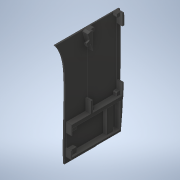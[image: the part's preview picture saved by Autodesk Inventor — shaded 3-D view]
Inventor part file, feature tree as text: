
AUTODESK INVENTOR PART (.ipt)
format: ipt  version: 2020.1 (Build 241239000, 239)  size: 1,676,800 bytes
history: native  units: mm
features: extrude x9, sketch x7, other x4, projected_geometry x3, split x1, chamfer x1, surface_op x1
ambient origin geometry x8: Origin, YZ Plane, XZ Plane, XY Plane, X Axis, Y Axis, Z Axis, Center Point
bodies: Solid1 (feature_tree)
feature tree (26):
  other  "Remote Bottom Shell.ipt"
  sketch  "Sketch1"  dims[d0=10.0mm d1=18.1mm]
  extrude  "Extrusion2"  Depth=10.0mm
  extrude  "Extrusion4"  Depth=29.5mm
  sketch  "Sketch3"  dims[d2=43.6mm d5=29.5mm]
  extrude  "Extrusion5"  Depth=2.0mm
  extrude  "Extrusion6"  Depth=1.2mm
  extrude  "Extrusion7"  Depth=1.2mm
  split  "Split1"
  extrude  "Extrusion8"  Depth=1.4mm
  extrude  "Extrusion9"  Depth=10.0mm
  extrude  "Extrusion10"  Depth=10.0mm TaperAngle=0.0deg
  chamfer  "Chamfer1"  Distance=3.5mm
  extrude  "Extrusion11"  Depth=10.0mm
  other  "Plate Solid::Remote Bottom Shell.ipt"
  other  "TaggingFeature1"
  projected_geometry  "Projected Loop1"
  sketch  "Sketch4"  dims[d6=15.35mm d7=2.0mm]
  sketch  "Sketch5"  dims[d8=0.2mm d9=0.0mm d17=1.2mm]
  projected_geometry  "Projected Loop2"
  projected_geometry  "Projected Loop3"
  sketch  "Sketch6"  dims[d18=1.2mm d21=30.0mm]
  sketch  "Sketch7"  dims[d22=3.3mm d23=0.0mm d26=1.4mm]
  sketch  "Sketch8"  dims[d27=15.22mm d28=40.66mm d29=2.2mm d30=0.0mm d31=3.5mm d32=0.0mm d33=4.0mm d34=3.0mm d43=2.2mm d44=0.0mm d45=4.0mm d46=3.0mm d47=0.8mm d48=10.0mm d49=0.0mm d51=2.904437mm d52=10.0mm d53=0.0mm d54=0.3mm d55=0.3mm d56=10.0mm d57=0.0mm d58=4.0mm d59=0.3mm d60=45.0deg d61=8.0mm d62=1.3mm d63=0.2mm d64=8.0mm d65=2.4mm d67=2.0mm d68=0.0mm d70=5.5mm d73=1.5mm]
  surface_op  "Surface1"
  other  "Srf1"
